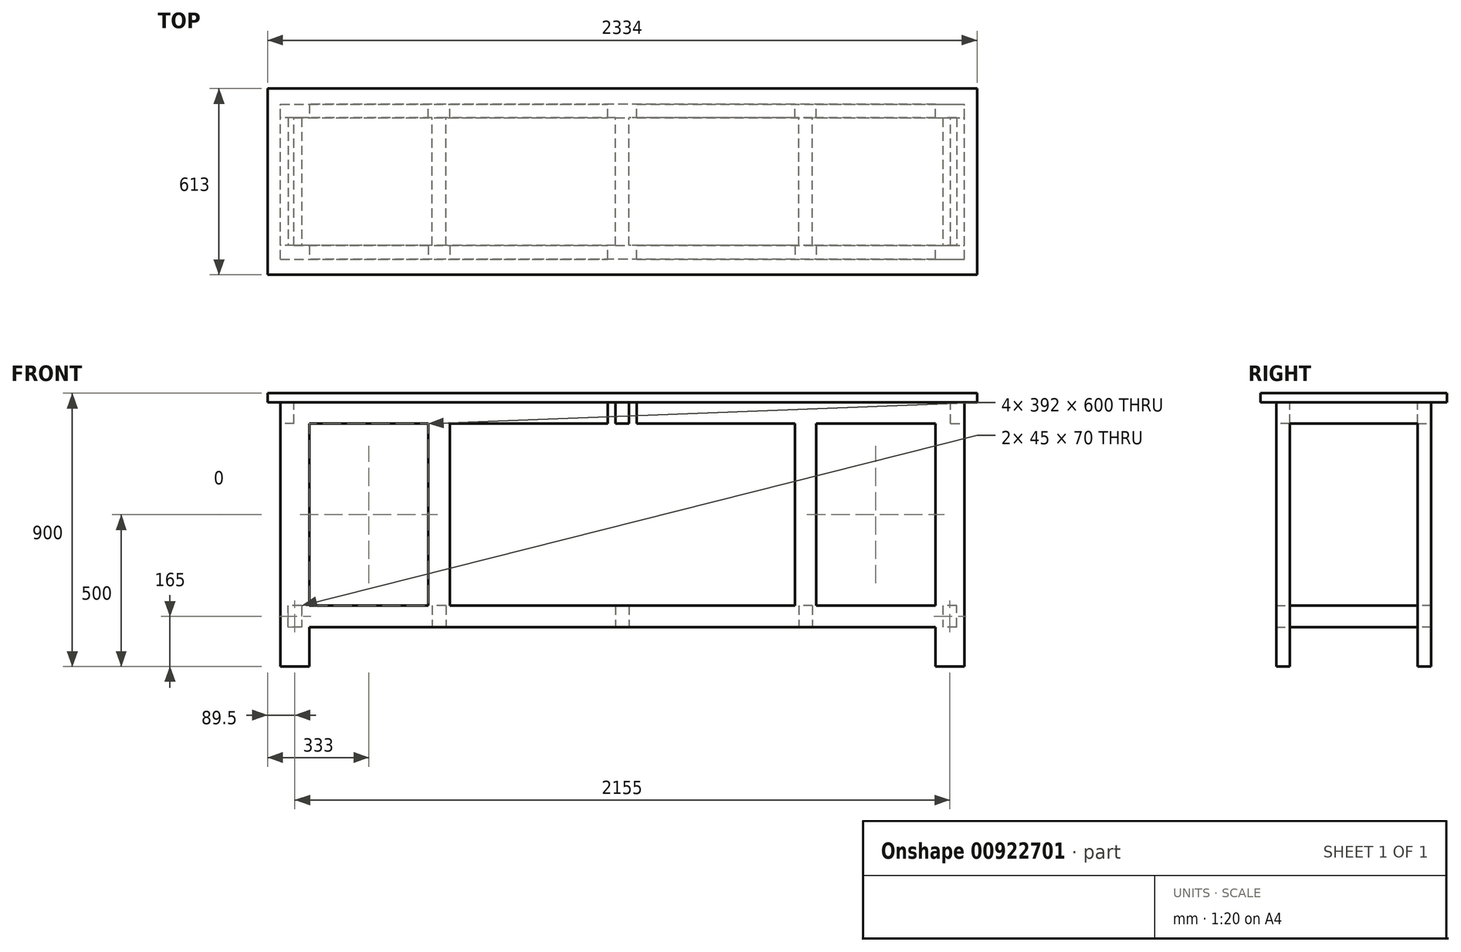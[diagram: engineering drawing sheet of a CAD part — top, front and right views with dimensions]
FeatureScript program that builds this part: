
annotation { "Feature Type Name" : "Feature", "Feature Type Description" : "" }
export const myFeature = defineFeature(function(context is Context, id is Id, definition is map)
    precondition{}
    {
        {
            var Q0;
            Q0=qCreatedBy(makeId("Top.planeOp"),FACE);
            cPlane(context, id + "F0", {"entities" : qUnion([Q0]), "cplaneType" : CPlaneType.OFFSET, "offset" : 900 * mm, "width" : 150 * mm, "height" : 150 * mm});
        }
        {
            var Q0;
            Q0=qCreatedBy(id+"F0.planeOp",FACE);
            var sketch = newSketch(context, id + "F1", { "sketchPlane" : qUnion([Q0])});
            skLineSegment(sketch, "E0.bottom", {"start": v(1167, -306.5) * mm, "end": v(-1167, -306.5) * mm});
            skLineSegment(sketch, "E0.top", {"start": v(1167, 306.5) * mm, "end": v(-1167, 306.5) * mm});
            skLineSegment(sketch, "E0.left", {"start": v(1167, -306.5) * mm, "end": v(1167, 306.5) * mm});
            skLineSegment(sketch, "E0.right", {"start": v(-1167, -306.5) * mm, "end": v(-1167, 306.5) * mm});
            skPoint(sketch, "E0.middle", {"position": v(0, 0) * mm});
            skSolve(sketch);
        }
        {
            var Q0;
            Q0=makeQuery(id+"F1.imprint","IMPRINT",FACE,{"disambiguationData":[TD([[makeQuery(id+"F1.imprint","IMPRINT",EDGE,{"derivedFrom":sQuery(id+"F1.wireOp",EDGE,"E0.bottom")}),-1.0]])]});
            extrude(context, id + "F2", {"entities" : qUnion([Q0]), "oppositeDirection" : true, "depth" : 30 * mm, "offsetDistance" : 25 * mm});
        }
        {
            var Q0;
            Q0=makeQuery(id+"F2.opExtrude","CAP_FACE",FACE,{"disambiguationData":[OSD([sQuery(id+"F1.wireOp",EDGE,"E0.bottom"),sQuery(id+"F1.wireOp",EDGE,"E0.top"),sQuery(id+"F1.wireOp",EDGE,"E0.left"),sQuery(id+"F1.wireOp",EDGE,"E0.right")])],"isStart":false});
            var sketch = newSketch(context, id + "F3", { "sketchPlane" : qUnion([Q0])});
            skLineSegment(sketch, "E1.bottom", {"start": v(-1125, 255) * mm, "end": v(1125, 255) * mm});
            skLineSegment(sketch, "E1.top", {"start": v(-1125, -255) * mm, "end": v(1125, -255) * mm});
            skLineSegment(sketch, "E1.left", {"start": v(-1125, 255) * mm, "end": v(-1125, -255) * mm});
            skLineSegment(sketch, "E1.right", {"start": v(1125, 255) * mm, "end": v(1125, -255) * mm});
            skPoint(sketch, "E1.middle", {"position": v(0, 0) * mm});
            skLineSegment(sketch, "E2.bottom", {"start": v(-1080, 210) * mm, "end": v(1080, 210) * mm});
            skLineSegment(sketch, "E2.top", {"start": v(-1080, -210) * mm, "end": v(1080, -210) * mm});
            skLineSegment(sketch, "E2.left", {"start": v(-1080, 210) * mm, "end": v(-1080, -210) * mm});
            skLineSegment(sketch, "E2.right", {"start": v(1080, 210) * mm, "end": v(1080, -210) * mm});
            skLineSegment(sketch, "E3", {"start": v(-1080, 210) * mm, "end": v(-1125, 210) * mm});
            skPoint(sketch, "E4", {"position": v(-1030, 210) * mm});
            skLineSegment(sketch, "E5", {"start": v(-1030, 210) * mm, "end": v(-1030, 255) * mm});
            skLineSegment(sketch, "E6", {"start": v(0, 0) * mm, "end": v(0, 95) * mm, "construction": true});
            skLineSegment(sketch, "E7", {"start": v(0, 0) * mm, "end": v(-86.34, 0) * mm, "construction": true});
            skLineSegment(sketch, "E8.MirrorCS", {"start": v(-1080, -210) * mm, "end": v(-1125, -210) * mm});
            skLineSegment(sketch, "E9.MirrorCS", {"start": v(-1030, -210) * mm, "end": v(-1030, -255) * mm});
            skLineSegment(sketch, "E10.MirrorCS", {"start": v(1030, 210) * mm, "end": v(1030, 255) * mm});
            skLineSegment(sketch, "E11.MirrorCS", {"start": v(1080, 210) * mm, "end": v(1125, 210) * mm});
            skLineSegment(sketch, "E12.MirrorCS", {"start": v(1030, -210) * mm, "end": v(1030, -255) * mm});
            skLineSegment(sketch, "E13.MirrorCS", {"start": v(1080, -210) * mm, "end": v(1125, -210) * mm});
            skLineSegment(sketch, "E14.bottom", {"start": v(22.5, 210) * mm, "end": v(-22.5, 210) * mm});
            skLineSegment(sketch, "E14.top", {"start": v(22.5, -210) * mm, "end": v(-22.5, -210) * mm});
            skLineSegment(sketch, "E14.left", {"start": v(22.5, 210) * mm, "end": v(22.5, -210) * mm});
            skLineSegment(sketch, "E14.right", {"start": v(-22.5, 210) * mm, "end": v(-22.5, -210) * mm});
            skPoint(sketch, "E15.oppositeSnap0", {"position": v(0, 47.5) * mm});
            skLineSegment(sketch, "E15.left", {"start": v(22.5, -47.5) * mm, "end": v(22.5, 47.5) * mm});
            skLineSegment(sketch, "E16", {"start": v(0, -210) * mm, "end": v(0, -255) * mm, "construction": true});
            skLineSegment(sketch, "E17", {"start": v(0, 210) * mm, "end": v(0, 255) * mm, "construction": true});
            skLineSegment(sketch, "E18.bottom", {"start": v(47.5, 255) * mm, "end": v(-47.5, 255) * mm});
            skLineSegment(sketch, "E18.top", {"start": v(47.5, 210) * mm, "end": v(-47.5, 210) * mm});
            skLineSegment(sketch, "E18.left", {"start": v(47.5, 255) * mm, "end": v(47.5, 210) * mm});
            skLineSegment(sketch, "E18.right", {"start": v(-47.5, 255) * mm, "end": v(-47.5, 210) * mm});
            skPoint(sketch, "E18.middle", {"position": v(0, 232.5) * mm});
            skLineSegment(sketch, "E19.bottom", {"start": v(47.5, -210) * mm, "end": v(-47.5, -210) * mm});
            skLineSegment(sketch, "E19.top", {"start": v(47.5, -255) * mm, "end": v(-47.5, -255) * mm});
            skLineSegment(sketch, "E19.left", {"start": v(47.5, -210) * mm, "end": v(47.5, -255) * mm});
            skLineSegment(sketch, "E19.right", {"start": v(-47.5, -210) * mm, "end": v(-47.5, -255) * mm});
            skPoint(sketch, "E19.middle", {"position": v(0, -232.5) * mm});
            skSolve(sketch);
        }
        {
            var Q0;
            Q0=makeQuery(id+"F3.imprint","IMPRINT",FACE,{"disambiguationData":[TD([[makeQuery(id+"F3.imprint","IMPRINT",EDGE,{"derivedFrom":sQuery(id+"F3.wireOp",EDGE,"E2.left")}),-1.0]])]});
            var Q1;
            Q1=makeQuery(id+"F3.imprint","IMPRINT",FACE,{"disambiguationData":[TD([[makeQuery(id+"F3.imprint","IMPRINT",EDGE,{"derivedFrom":sQuery(id+"F3.wireOp",EDGE,"E2.right")}),1.0]])]});
            var Q2;
            {var subQ3=sQuery(id+"F3.wireOp",EDGE,"E5");Q2=makeQuery(id+"F3.imprint","IMPRINT",FACE,{"disambiguationData":[TD([[makeQuery(id+"F3.imprint","IMPRINT",EDGE,{"derivedFrom":subQ3}),-1.0]])]});}
            var Q3;
            {var subQ0=sQuery(id+"F3.wireOp",EDGE,"E9.MirrorCS");Q3=makeQuery(id+"F3.imprint","IMPRINT",FACE,{"disambiguationData":[TD([[makeQuery(id+"F3.imprint","IMPRINT",EDGE,{"derivedFrom":subQ0}),1.0]])]});}
            var Q4;
            {var subQ3=sQuery(id+"F3.wireOp",EDGE,"E14.bottom");Q4=makeQuery(id+"F3.imprint","IMPRINT",FACE,{"disambiguationData":[TD([[makeQuery(id+"F3.imprint","IMPRINT",EDGE,{"derivedFrom":subQ3}),1.0]])]});}
            var Q5;
            {var subQ0=sQuery(id+"F3.wireOp",EDGE,"E10.MirrorCS");Q5=makeQuery(id+"F3.imprint","IMPRINT",FACE,{"disambiguationData":[TD([[makeQuery(id+"F3.imprint","IMPRINT",EDGE,{"derivedFrom":subQ0}),1.0]])]});}
            var Q6;
            {var subQ1=sQuery(id+"F3.wireOp",EDGE,"E14.right");Q6=makeQuery(id+"F3.imprint","IMPRINT",FACE,{"disambiguationData":[TD([[makeQuery(id+"F3.imprint","IMPRINT",EDGE,{"derivedFrom":subQ1}),1.0]])]});}
            var Q7;
            {var subQ0=sQuery(id+"F3.wireOp",EDGE,"E12.MirrorCS");Q7=makeQuery(id+"F3.imprint","IMPRINT",FACE,{"disambiguationData":[TD([[makeQuery(id+"F3.imprint","IMPRINT",EDGE,{"derivedFrom":subQ0}),-1.0]])]});}
            extrude(context, id + "F4", {"entities" : qUnion([Q0, Q1, Q2, Q3, Q4, Q5, Q6, Q7]), "operationType" : NewBodyOperationType.ADD, "depth" : 70 * mm, "offsetDistance" : 25 * mm});
        }
        {
            var Q0;
            {var subQ0=sQuery(id+"F3.wireOp",EDGE,"E3");Q0=makeQuery(id+"F3.imprint","IMPRINT",FACE,{"disambiguationData":[TD([[makeQuery(id+"F3.imprint","IMPRINT",EDGE,{"derivedFrom":subQ0}),-1.0]])]});}
            var Q1;
            {var subQ0=sQuery(id+"F3.wireOp",EDGE,"E8.MirrorCS");Q1=makeQuery(id+"F3.imprint","IMPRINT",FACE,{"disambiguationData":[TD([[makeQuery(id+"F3.imprint","IMPRINT",EDGE,{"derivedFrom":subQ0}),1.0]])]});}
            var Q2;
            {var subQ0=sQuery(id+"F3.wireOp",EDGE,"E12.MirrorCS");Q2=makeQuery(id+"F3.imprint","IMPRINT",FACE,{"disambiguationData":[TD([[makeQuery(id+"F3.imprint","IMPRINT",EDGE,{"derivedFrom":subQ0}),1.0]])]});}
            var Q3;
            {var subQ0=sQuery(id+"F3.wireOp",EDGE,"E10.MirrorCS");Q3=makeQuery(id+"F3.imprint","IMPRINT",FACE,{"disambiguationData":[TD([[makeQuery(id+"F3.imprint","IMPRINT",EDGE,{"derivedFrom":subQ0}),-1.0]])]});}
            var Q4;
            Q4=makeQuery(id+"F3.imprint","IMPRINT",FACE,{"disambiguationData":[TD([[makeQuery(id+"F3.imprint","IMPRINT",EDGE,{"derivedFrom":sQuery(id+"F3.wireOp",EDGE,"E15.bottom")}),1.0]])]});
            var Q5;
            Q5=makeQuery(id+"F3.imprint","IMPRINT",FACE,{"disambiguationData":[TD([[makeQuery(id+"F3.imprint","IMPRINT",EDGE,{"derivedFrom":sQuery(id+"F3.wireOp",EDGE,"E18.bottom")}),1.0]])]});
            var Q6;
            Q6=makeQuery(id+"F3.imprint","IMPRINT",FACE,{"disambiguationData":[TD([[makeQuery(id+"F3.imprint","IMPRINT",EDGE,{"derivedFrom":sQuery(id+"F3.wireOp",EDGE,"E19.top")}),-1.0]])]});
            extrude(context, id + "F5", {"entities" : qUnion([Q0, Q1, Q2, Q3, Q4, Q5, Q6]), "operationType" : NewBodyOperationType.ADD, "depth" : (900 - 30) * mm, "offsetDistance" : 25 * mm});
        }
        {
            var Q0;
            Q0=qCreatedBy(makeId("Top.planeOp"),FACE);
            cPlane(context, id + "F6", {"entities" : qUnion([Q0]), "cplaneType" : CPlaneType.OFFSET, "offset" : 130 * mm, "width" : 150 * mm, "height" : 150 * mm});
        }
        {
            var Q0;
            Q0=qCreatedBy(makeId("Top.planeOp"),FACE);
            cPlane(context, id + "F7", {"entities" : qUnion([Q0]), "cplaneType" : CPlaneType.OFFSET, "offset" : 400 * mm, "width" : 150 * mm, "height" : 150 * mm});
        }
        {
            var Q0;
            Q0=qCreatedBy(id+"F6.planeOp",FACE);
            var sketch = newSketch(context, id + "F8", { "sketchPlane" : qUnion([Q0])});
            skLineSegment(sketch, "E20.bottom", {"start": v(1100, 255) * mm, "end": v(-1100, 255) * mm});
            skLineSegment(sketch, "E20.top", {"start": v(1100, -255) * mm, "end": v(-1100, -255) * mm});
            skLineSegment(sketch, "E20.left", {"start": v(1100, 255) * mm, "end": v(1100, -255) * mm});
            skLineSegment(sketch, "E20.right", {"start": v(-1100, 255) * mm, "end": v(-1100, -255) * mm});
            skPoint(sketch, "E20.middle", {"position": v(0, 0) * mm});
            skLineSegment(sketch, "E21.bottom", {"start": v(1055, 210) * mm, "end": v(-1055, 210) * mm});
            skLineSegment(sketch, "E21.top", {"start": v(1055, -210) * mm, "end": v(-1055, -210) * mm});
            skLineSegment(sketch, "E21.left", {"start": v(1055, 210) * mm, "end": v(1055, -210) * mm});
            skLineSegment(sketch, "E21.right", {"start": v(-1055, 210) * mm, "end": v(-1055, -210) * mm});
            skLineSegment(sketch, "E22.bottom", {"start": v(22.5, 210) * mm, "end": v(-22.5, 210) * mm});
            skLineSegment(sketch, "E22.top", {"start": v(22.5, -210) * mm, "end": v(-22.5, -210) * mm});
            skLineSegment(sketch, "E22.left", {"start": v(22.5, 210) * mm, "end": v(22.5, -210) * mm});
            skLineSegment(sketch, "E22.right", {"start": v(-22.5, 210) * mm, "end": v(-22.5, -210) * mm});
            skLineSegment(sketch, "E23.bottom", {"start": v(-638, -255) * mm, "end": v(-568, -255) * mm});
            skLineSegment(sketch, "E23.top", {"start": v(-638, -210) * mm, "end": v(-568, -210) * mm});
            skLineSegment(sketch, "E23.left", {"start": v(-638, -255) * mm, "end": v(-638, -210) * mm});
            skLineSegment(sketch, "E23.right", {"start": v(-568, -255) * mm, "end": v(-568, -210) * mm});
            skLineSegment(sketch, "E24", {"start": v(0, -137.68) * mm, "end": v(0, 127.46) * mm, "construction": true});
            skLineSegment(sketch, "E25", {"start": v(-110.43, 0) * mm, "end": v(123, 0) * mm, "construction": true});
            skLineSegment(sketch, "E26.MirrorCS", {"start": v(-568, 255) * mm, "end": v(-568, 210) * mm});
            skLineSegment(sketch, "E27.MirrorCS", {"start": v(-638, 255) * mm, "end": v(-638, 210) * mm});
            skLineSegment(sketch, "E28.MirrorCS", {"start": v(-638, 210) * mm, "end": v(-568, 210) * mm});
            skLineSegment(sketch, "E29.MirrorCS", {"start": v(-638, 255) * mm, "end": v(-568, 255) * mm});
            skLineSegment(sketch, "E30.MirrorCS", {"start": v(638, 255) * mm, "end": v(638, 210) * mm});
            skLineSegment(sketch, "E31.MirrorCS", {"start": v(638, 255) * mm, "end": v(568, 255) * mm});
            skLineSegment(sketch, "E32.MirrorCS", {"start": v(638, 210) * mm, "end": v(568, 210) * mm});
            skLineSegment(sketch, "E33.MirrorCS", {"start": v(568, 255) * mm, "end": v(568, 210) * mm});
            skLineSegment(sketch, "E34.MirrorCS", {"start": v(638, -255) * mm, "end": v(638, -210) * mm});
            skLineSegment(sketch, "E35.MirrorCS", {"start": v(638, -210) * mm, "end": v(568, -210) * mm});
            skLineSegment(sketch, "E36.MirrorCS", {"start": v(638, -255) * mm, "end": v(568, -255) * mm});
            skLineSegment(sketch, "E37.MirrorCS", {"start": v(568, -255) * mm, "end": v(568, -210) * mm});
            skLineSegment(sketch, "E38.bottom", {"start": v(-625.5, -210) * mm, "end": v(-580.5, -210) * mm});
            skLineSegment(sketch, "E38.top", {"start": v(-625.5, 210) * mm, "end": v(-580.5, 210) * mm});
            skLineSegment(sketch, "E38.left", {"start": v(-625.5, -210) * mm, "end": v(-625.5, 210) * mm});
            skLineSegment(sketch, "E38.right", {"start": v(-580.5, -210) * mm, "end": v(-580.5, 210) * mm});
            skLineSegment(sketch, "E39.MirrorCS", {"start": v(625.5, -210) * mm, "end": v(580.5, -210) * mm});
            skLineSegment(sketch, "E40.MirrorCS", {"start": v(625.5, 210) * mm, "end": v(580.5, 210) * mm});
            skLineSegment(sketch, "E41.MirrorCS", {"start": v(625.5, -210) * mm, "end": v(625.5, 210) * mm});
            skLineSegment(sketch, "E42.MirrorCS", {"start": v(580.5, -210) * mm, "end": v(580.5, 210) * mm});
            skSolve(sketch);
        }
        {
            var Q0;
            {var subQ3=sQuery(id+"F8.wireOp",EDGE,"E20.right");Q0=makeQuery(id+"F8.imprint","IMPRINT",FACE,{"disambiguationData":[TD([[makeQuery(id+"F8.imprint","IMPRINT",EDGE,{"derivedFrom":subQ3}),1.0]])]});}
            var Q1;
            {var subQ2=sQuery(id+"F8.wireOp",EDGE,"E26.MirrorCS");Q1=makeQuery(id+"F8.imprint","IMPRINT",FACE,{"disambiguationData":[TD([[makeQuery(id+"F8.imprint","IMPRINT",EDGE,{"derivedFrom":subQ2}),1.0]])]});}
            var Q2;
            {var subQ2=sQuery(id+"F8.wireOp",EDGE,"E23.right");Q2=makeQuery(id+"F8.imprint","IMPRINT",FACE,{"disambiguationData":[TD([[makeQuery(id+"F8.imprint","IMPRINT",EDGE,{"derivedFrom":subQ2}),-1.0]])]});}
            var Q3;
            {var subQ0=sQuery(id+"F8.wireOp",EDGE,"E22.left");Q3=makeQuery(id+"F8.imprint","IMPRINT",FACE,{"disambiguationData":[TD([[makeQuery(id+"F8.imprint","IMPRINT",EDGE,{"derivedFrom":subQ0}),-1.0]])]});}
            var Q4;
            {var subQ3=sQuery(id+"F8.wireOp",EDGE,"E20.left");Q4=makeQuery(id+"F8.imprint","IMPRINT",FACE,{"disambiguationData":[TD([[makeQuery(id+"F8.imprint","IMPRINT",EDGE,{"derivedFrom":subQ3}),-1.0]])]});}
            extrude(context, id + "F9", {"entities" : qUnion([Q0, Q1, Q2, Q3, Q4]), "operationType" : NewBodyOperationType.ADD, "depth" : 70 * mm, "offsetDistance" : 25 * mm});
        }
        {
            var Q0;
            {var subQ3=sQuery(id+"F8.wireOp",EDGE,"E23.left");Q0=makeQuery(id+"F8.imprint","IMPRINT",FACE,{"disambiguationData":[TD([[makeQuery(id+"F8.imprint","IMPRINT",EDGE,{"derivedFrom":subQ3}),-1.0]])]});}
            var Q1;
            {var subQ0=sQuery(id+"F8.wireOp",EDGE,"E26.MirrorCS");Q1=makeQuery(id+"F8.imprint","IMPRINT",FACE,{"disambiguationData":[TD([[makeQuery(id+"F8.imprint","IMPRINT",EDGE,{"derivedFrom":subQ0}),-1.0]])]});}
            var Q2;
            {var subQ3=sQuery(id+"F8.wireOp",EDGE,"E30.MirrorCS");Q2=makeQuery(id+"F8.imprint","IMPRINT",FACE,{"disambiguationData":[TD([[makeQuery(id+"F8.imprint","IMPRINT",EDGE,{"derivedFrom":subQ3}),-1.0]])]});}
            var Q3;
            {var subQ0=sQuery(id+"F8.wireOp",EDGE,"E34.MirrorCS");Q3=makeQuery(id+"F8.imprint","IMPRINT",FACE,{"disambiguationData":[TD([[makeQuery(id+"F8.imprint","IMPRINT",EDGE,{"derivedFrom":subQ0}),1.0]])]});}
            var Q4;
            Q4=makeQuery(id+"F4.opExtrude","CAP_FACE",FACE,{"disambiguationData":[OSD([sQuery(id+"F3.wireOp",EDGE,"E1.bottom"),sQuery(id+"F3.wireOp",EDGE,"E2.bottom"),sQuery(id+"F3.wireOp",EDGE,"E5"),sQuery(id+"F3.wireOp",EDGE,"E18.right")])],"isStart":false});
            extrude(context, id + "F10", {"entities" : qUnion([Q0, Q1, Q2, Q3]), "operationType" : NewBodyOperationType.ADD, "endBound" : BoundingType.UP_TO_SURFACE, "depth" : 25 * mm, "endBoundEntityFace" : qUnion([Q4]), "offsetDistance" : 25 * mm});
        }
        {
            var Q0;
            {var subQ0=sQuery(id+"F8.wireOp",EDGE,"E38.left");Q0=makeQuery(id+"F8.imprint","IMPRINT",FACE,{"disambiguationData":[TD([[makeQuery(id+"F8.imprint","IMPRINT",EDGE,{"derivedFrom":subQ0}),-1.0]])]});}
            var Q1;
            {var subQ0=sQuery(id+"F8.wireOp",EDGE,"E41.MirrorCS");Q1=makeQuery(id+"F8.imprint","IMPRINT",FACE,{"disambiguationData":[TD([[makeQuery(id+"F8.imprint","IMPRINT",EDGE,{"derivedFrom":subQ0}),1.0]])]});}
            extrude(context, id + "F11", {"entities" : qUnion([Q0, Q1]), "operationType" : NewBodyOperationType.ADD, "depth" : 70 * mm, "offsetDistance" : 25 * mm});
        }
    });
